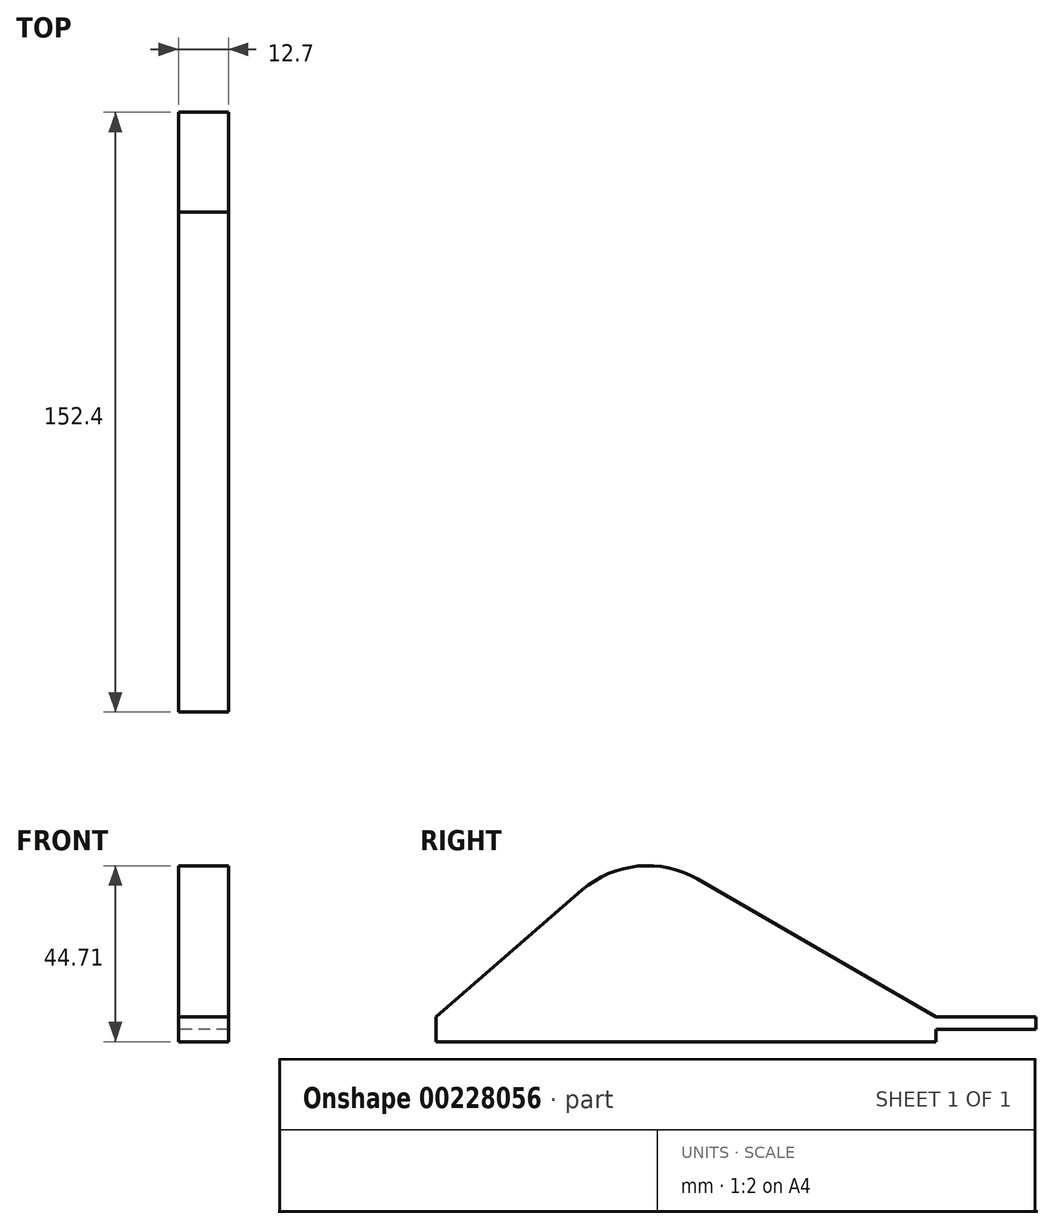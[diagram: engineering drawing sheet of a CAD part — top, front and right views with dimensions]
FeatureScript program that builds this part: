
annotation { "Feature Type Name" : "Feature", "Feature Type Description" : "" }
export const myFeature = defineFeature(function(context is Context, id is Id, definition is map)
    precondition{}
    {
        {
            var Q0;
            Q0=qCreatedBy(makeId("Right.planeOp"),FACE);
            var sketch = newSketch(context, id + "F0", { "sketchPlane" : qUnion([Q0])});
            skLineSegment(sketch, "E0", {"start": v(0, 0) * mm, "end": v(127, 0) * mm});
            skLineSegment(sketch, "E1", {"start": v(0, 0) * mm, "end": v(0, 6.35) * mm});
            skLineSegment(sketch, "E2", {"start": v(0, 6.35) * mm, "end": v(50.8, 50.34) * mm});
            skLineSegment(sketch, "E3", {"start": v(50.8, 50.34) * mm, "end": v(50.8, 0) * mm, "construction": true});
            skLineSegment(sketch, "E4", {"start": v(50.8, 50.34) * mm, "end": v(127, 6.35) * mm});
            skLineSegment(sketch, "E5", {"start": v(127, 6.35) * mm, "end": v(127, 0) * mm});
            skSolve(sketch);
        }
        {
            var Q0;
            Q0 = qSketchRegion(id + "F0", true);
            extrude(context, id + "F1", {"entities" : qUnion([Q0]), "depth" : 12.7 * mm, "offsetDistance" : 25.4 * mm});
        }
        {
            var Q0;
            Q0=makeQuery(id+"F1.opExtrude","SWEPT_EDGE",EDGE,{"disambiguationData":[OSD([sQuery(id+"F0.wireOp",EDGE,"E2"),sQuery(id+"F0.wireOp",EDGE,"E4")])]});
            fillet(context, id + "F2", {"entities" : qUnion([Q0]), "radius" : 25.4 * mm, "tangentPropagation" : true, "allowEdgeOverflow" : false});
        }
        {
            var Q0;
            Q0=makeQuery(id+"F1.opExtrude","SWEPT_FACE",FACE,{"disambiguationData":[OSD([sQuery(id+"F0.wireOp",EDGE,"E5")])]});
            var sketch = newSketch(context, id + "F3", { "sketchPlane" : qUnion([Q0])});
            skLineSegment(sketch, "E6.bottom", {"start": v(-12.7, 6.35) * mm, "end": v(0, 6.35) * mm});
            skLineSegment(sketch, "E6.top", {"start": v(-12.7, 3.18) * mm, "end": v(0, 3.18) * mm});
            skLineSegment(sketch, "E6.left", {"start": v(-12.7, 6.35) * mm, "end": v(-12.7, 3.18) * mm});
            skLineSegment(sketch, "E6.right", {"start": v(0, 6.35) * mm, "end": v(0, 3.18) * mm});
            skSolve(sketch);
        }
        {
            var Q0;
            Q0 = qSketchRegion(id + "F3", true);
            extrude(context, id + "F4", {"entities" : qUnion([Q0]), "operationType" : NewBodyOperationType.ADD, "depth" : 25.4 * mm, "offsetDistance" : 25.4 * mm});
        }
    });
